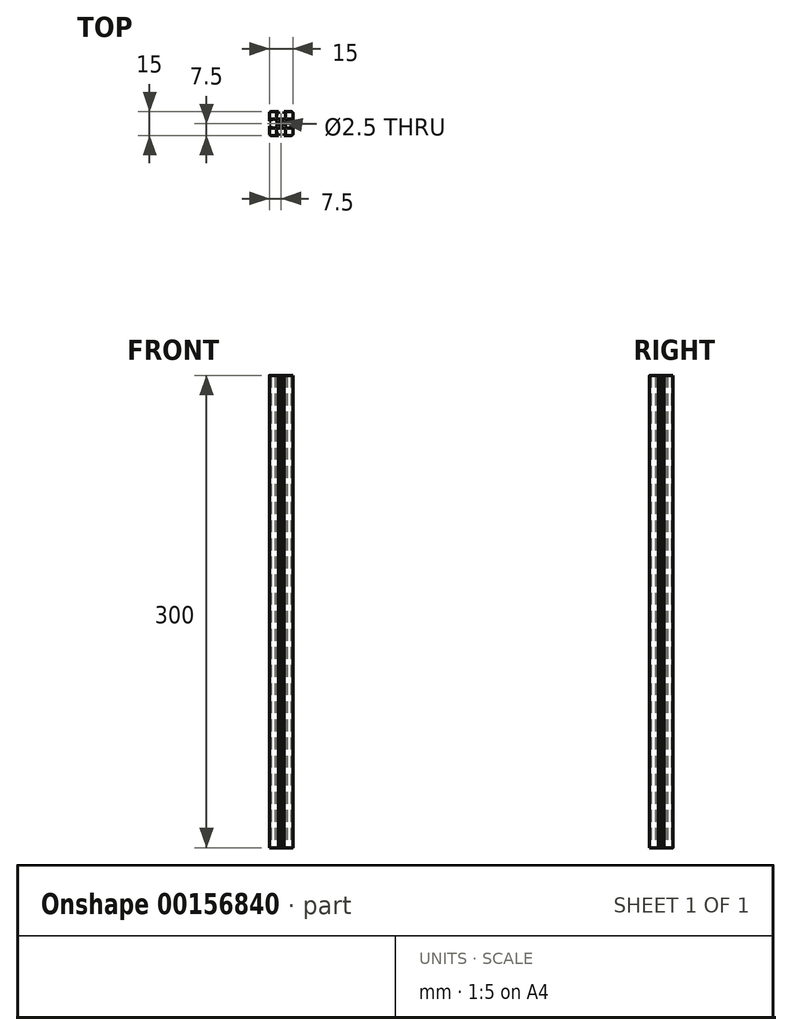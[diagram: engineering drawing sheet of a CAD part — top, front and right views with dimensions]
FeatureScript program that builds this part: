
annotation { "Feature Type Name" : "Feature", "Feature Type Description" : "" }
export const myFeature = defineFeature(function(context is Context, id is Id, definition is map)
    precondition{}
    {
        {
            var Q0;
            Q0=qCreatedBy(makeId("Top.planeOp"),FACE);
            var sketch = newSketch(context, id + "F0", { "sketchPlane" : qUnion([Q0])});
            skLineSegment(sketch, "E0.bottom", {"start": v(6.5, -7.5) * mm, "end": v(1.7, -7.5) * mm});
            skLineSegment(sketch, "E0.top", {"start": v(6.5, 7.5) * mm, "end": v(1.7, 7.5) * mm});
            skLineSegment(sketch, "E0.left", {"start": v(7.5, -6.5) * mm, "end": v(7.5, -1.7) * mm});
            skLineSegment(sketch, "E0.right", {"start": v(-7.5, -6.5) * mm, "end": v(-7.5, -1.7) * mm});
            skPoint(sketch, "E0.middle", {"position": v(0, 0) * mm});
            skPoint(sketch, "E1.visualSharp", {"position": v(7.5, 7.5) * mm});
            skArc(sketch, "E1.filletArc", {"start": v(7.5, 6.5) * mm, "mid": v(7.2, 7.2) * mm, "end": v(6.5, 7.5) * mm});
            skPoint(sketch, "E2.visualSharp", {"position": v(-7.5, 7.5) * mm});
            skArc(sketch, "E2.filletArc", {"start": v(-6.5, 7.5) * mm, "mid": v(-7.2, 7.2) * mm, "end": v(-7.5, 6.5) * mm});
            skPoint(sketch, "E3.visualSharp", {"position": v(-7.5, -7.5) * mm});
            skArc(sketch, "E3.filletArc", {"start": v(-7.5, -6.5) * mm, "mid": v(-7.2, -7.2) * mm, "end": v(-6.5, -7.5) * mm});
            skPoint(sketch, "E4.visualSharp", {"position": v(7.5, -7.5) * mm});
            skArc(sketch, "E4.filletArc", {"start": v(6.5, -7.5) * mm, "mid": v(7.2, -7.2) * mm, "end": v(7.5, -6.5) * mm});
            skCircle(sketch, "E5", {"center": v(0, 0) * mm, "radius": 1.25 * mm});
            skLineSegment(sketch, "E6", {"start": v(-1.7, 7.5) * mm, "end": v(-1.7, 6.4) * mm});
            skLineSegment(sketch, "E7", {"start": v(-1.7, 6.4) * mm, "end": v(-2.85, 6.4) * mm});
            skLineSegment(sketch, "E8", {"start": v(-2.85, 6.4) * mm, "end": v(-2.85, 3.8) * mm});
            skLineSegment(sketch, "E9", {"start": v(-2.85, 3.8) * mm, "end": v(-1.7, 2.8) * mm});
            skLineSegment(sketch, "E10", {"start": v(-1.7, 2.8) * mm, "end": v(-0.52, 2.8) * mm});
            skLineSegment(sketch, "E11", {"start": v(-0.52, 2.8) * mm, "end": v(0, 2.5) * mm});
            skLineSegment(sketch, "E12", {"start": v(0, 7.5) * mm, "end": v(0, 1.25) * mm, "construction": true});
            skLineSegment(sketch, "E13.MirrorCS", {"start": v(1.7, 7.5) * mm, "end": v(1.7, 6.4) * mm});
            skLineSegment(sketch, "E14.MirrorCS", {"start": v(1.7, 6.4) * mm, "end": v(2.85, 6.4) * mm});
            skLineSegment(sketch, "E15.MirrorCS", {"start": v(2.85, 6.4) * mm, "end": v(2.85, 3.8) * mm});
            skLineSegment(sketch, "E16.MirrorCS", {"start": v(2.85, 3.8) * mm, "end": v(1.7, 2.8) * mm});
            skLineSegment(sketch, "E17.MirrorCS", {"start": v(1.7, 2.8) * mm, "end": v(0.52, 2.8) * mm});
            skLineSegment(sketch, "E18.MirrorCS", {"start": v(0.52, 2.8) * mm, "end": v(0, 2.5) * mm});
            skLineSegment(sketch, "E19.1.0", {"start": v(-7.5, -1.7) * mm, "end": v(-6.4, -1.7) * mm});
            skLineSegment(sketch, "E19.1.1", {"start": v(-6.4, -1.7) * mm, "end": v(-6.4, -2.85) * mm});
            skLineSegment(sketch, "E19.1.2", {"start": v(-6.4, -2.85) * mm, "end": v(-3.8, -2.85) * mm});
            skLineSegment(sketch, "E19.1.3", {"start": v(-3.8, -2.85) * mm, "end": v(-2.8, -1.7) * mm});
            skLineSegment(sketch, "E19.1.4", {"start": v(-2.8, -1.7) * mm, "end": v(-2.8, -0.52) * mm});
            skLineSegment(sketch, "E19.1.5", {"start": v(-7.5, 1.7) * mm, "end": v(-6.4, 1.7) * mm});
            skLineSegment(sketch, "E19.1.6", {"start": v(-6.4, 1.7) * mm, "end": v(-6.4, 2.85) * mm});
            skLineSegment(sketch, "E19.1.7", {"start": v(-6.4, 2.85) * mm, "end": v(-3.8, 2.85) * mm});
            skLineSegment(sketch, "E19.1.8", {"start": v(-3.8, 2.85) * mm, "end": v(-2.8, 1.7) * mm});
            skLineSegment(sketch, "E19.1.9", {"start": v(-2.8, 1.7) * mm, "end": v(-2.8, 0.52) * mm});
            skLineSegment(sketch, "E19.1.10", {"start": v(-2.8, 0.52) * mm, "end": v(-2.5, 0) * mm});
            skLineSegment(sketch, "E19.1.11", {"start": v(-2.8, -0.52) * mm, "end": v(-2.5, 0) * mm});
            skLineSegment(sketch, "E19.2.0", {"start": v(1.7, -7.5) * mm, "end": v(1.7, -6.4) * mm});
            skLineSegment(sketch, "E19.2.1", {"start": v(1.7, -6.4) * mm, "end": v(2.85, -6.4) * mm});
            skLineSegment(sketch, "E19.2.2", {"start": v(2.85, -6.4) * mm, "end": v(2.85, -3.8) * mm});
            skLineSegment(sketch, "E19.2.3", {"start": v(2.85, -3.8) * mm, "end": v(1.7, -2.8) * mm});
            skLineSegment(sketch, "E19.2.4", {"start": v(1.7, -2.8) * mm, "end": v(0.52, -2.8) * mm});
            skLineSegment(sketch, "E19.2.5", {"start": v(-1.7, -7.5) * mm, "end": v(-1.7, -6.4) * mm});
            skLineSegment(sketch, "E19.2.6", {"start": v(-1.7, -6.4) * mm, "end": v(-2.85, -6.4) * mm});
            skLineSegment(sketch, "E19.2.7", {"start": v(-2.85, -6.4) * mm, "end": v(-2.85, -3.8) * mm});
            skLineSegment(sketch, "E19.2.8", {"start": v(-2.85, -3.8) * mm, "end": v(-1.7, -2.8) * mm});
            skLineSegment(sketch, "E19.2.9", {"start": v(-1.7, -2.8) * mm, "end": v(-0.52, -2.8) * mm});
            skLineSegment(sketch, "E19.2.10", {"start": v(-0.52, -2.8) * mm, "end": v(0, -2.5) * mm});
            skLineSegment(sketch, "E19.2.11", {"start": v(0.52, -2.8) * mm, "end": v(0, -2.5) * mm});
            skLineSegment(sketch, "E19.3.0", {"start": v(7.5, 1.7) * mm, "end": v(6.4, 1.7) * mm});
            skLineSegment(sketch, "E19.3.1", {"start": v(6.4, 1.7) * mm, "end": v(6.4, 2.85) * mm});
            skLineSegment(sketch, "E19.3.2", {"start": v(6.4, 2.85) * mm, "end": v(3.8, 2.85) * mm});
            skLineSegment(sketch, "E19.3.3", {"start": v(3.8, 2.85) * mm, "end": v(2.8, 1.7) * mm});
            skLineSegment(sketch, "E19.3.4", {"start": v(2.8, 1.7) * mm, "end": v(2.8, 0.52) * mm});
            skLineSegment(sketch, "E19.3.5", {"start": v(7.5, -1.7) * mm, "end": v(6.4, -1.7) * mm});
            skLineSegment(sketch, "E19.3.6", {"start": v(6.4, -1.7) * mm, "end": v(6.4, -2.85) * mm});
            skLineSegment(sketch, "E19.3.7", {"start": v(6.4, -2.85) * mm, "end": v(3.8, -2.85) * mm});
            skLineSegment(sketch, "E19.3.8", {"start": v(3.8, -2.85) * mm, "end": v(2.8, -1.7) * mm});
            skLineSegment(sketch, "E19.3.9", {"start": v(2.8, -1.7) * mm, "end": v(2.8, -0.52) * mm});
            skLineSegment(sketch, "E19.3.10", {"start": v(2.8, -0.52) * mm, "end": v(2.5, 0) * mm});
            skLineSegment(sketch, "E19.3.11", {"start": v(2.8, 0.52) * mm, "end": v(2.5, 0) * mm});
            skLineSegment(sketch, "E20.trimOffspring", {"start": v(-7.5, 1.7) * mm, "end": v(-7.5, 6.5) * mm});
            skLineSegment(sketch, "E21.trimOffspring", {"start": v(-1.7, -7.5) * mm, "end": v(-6.5, -7.5) * mm});
            skLineSegment(sketch, "E22.trimOffspring", {"start": v(7.5, 1.7) * mm, "end": v(7.5, 6.5) * mm});
            skLineSegment(sketch, "E23.trimOffspring", {"start": v(-1.7, 7.5) * mm, "end": v(-6.5, 7.5) * mm});
            skSolve(sketch);
        }
        {
            var Q0;
            Q0=qSketchRegion(id+"F0",true);
            extrude(context, id + "F1", {"entities" : qUnion([Q0]), "endBound" : BoundingType.SYMMETRIC, "depth" : 300 * mm});
        }
    });
